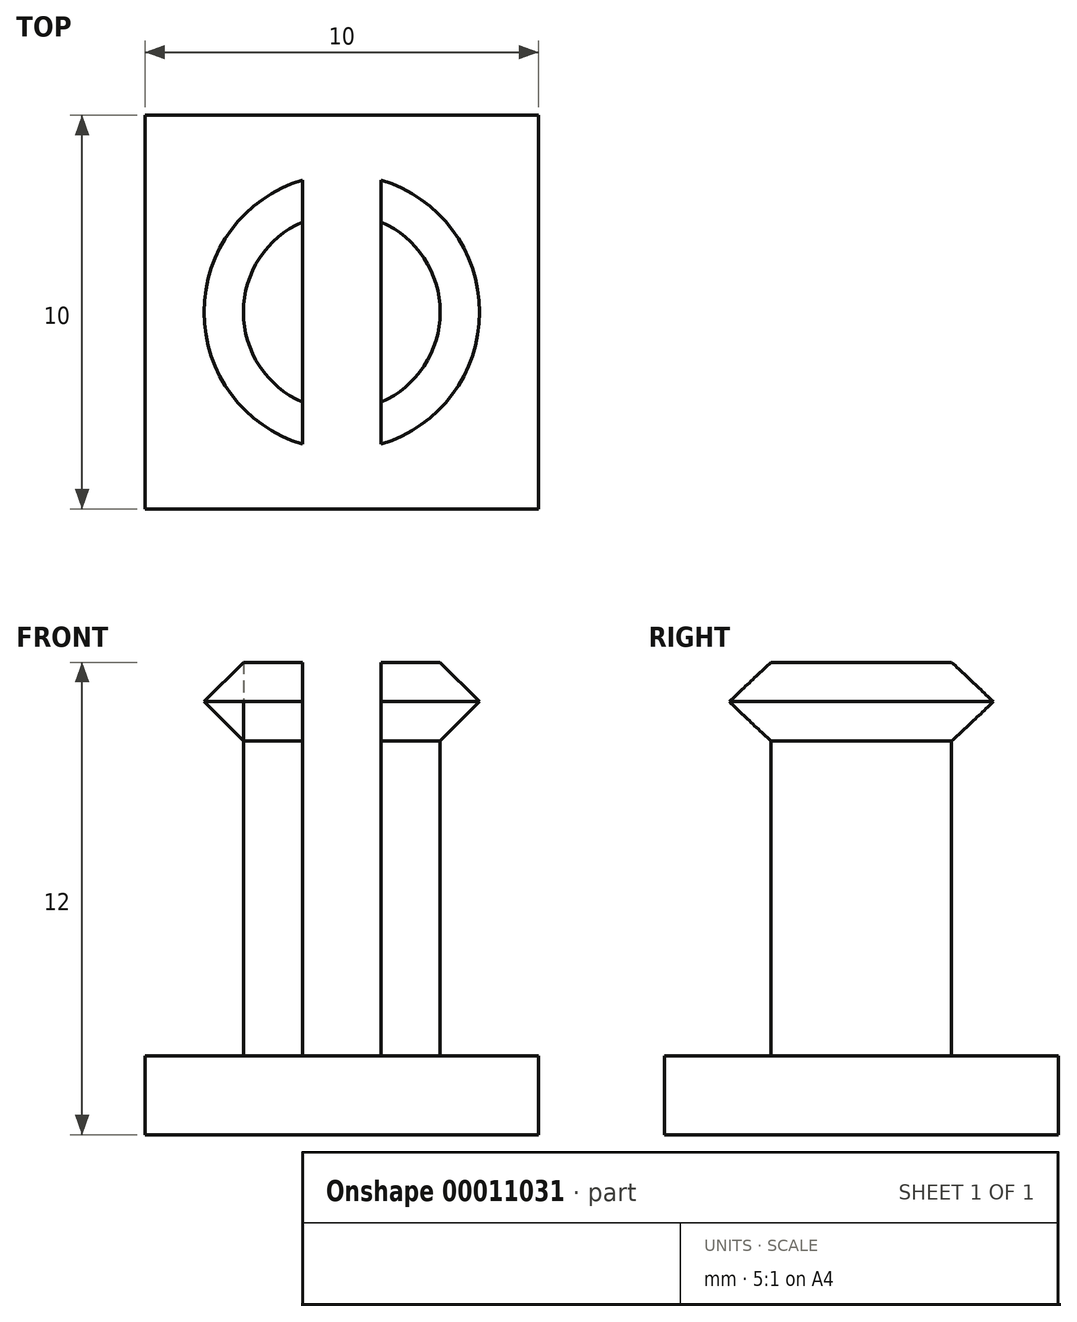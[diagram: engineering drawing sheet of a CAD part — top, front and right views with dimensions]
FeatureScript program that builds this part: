
annotation { "Feature Type Name" : "Feature", "Feature Type Description" : "" }
export const myFeature = defineFeature(function(context is Context, id is Id, definition is map)
    precondition{}
    {
        {
            var Q0;
            Q0=qCreatedBy(makeId("Top.planeOp"),FACE);
            var sketch = newSketch(context, id + "F0", { "sketchPlane" : qUnion([Q0])});
            skCircle(sketch, "E0", {"center": v(0, 0) * mm, "radius": 2.5 * mm});
            skLineSegment(sketch, "E1", {"start": v(0, 0) * mm, "end": v(-1, 0) * mm});
            skLineSegment(sketch, "E2", {"start": v(0, 0) * mm, "end": v(1, 0) * mm});
            skLineSegment(sketch, "E3", {"start": v(-1, 2.3) * mm, "end": v(-1, -2.3) * mm});
            skLineSegment(sketch, "E4", {"start": v(1, 2.3) * mm, "end": v(1, -2.3) * mm});
            skCircle(sketch, "E5.0", {"center": v(0, 0) * mm, "radius": 3.5 * mm});
            skLineSegment(sketch, "E6", {"start": v(-1, 2.3) * mm, "end": v(-1, 3.35) * mm});
            skLineSegment(sketch, "E7", {"start": v(1, 2.3) * mm, "end": v(1, 3.35) * mm});
            skLineSegment(sketch, "E8", {"start": v(1, -2.3) * mm, "end": v(1, -3.35) * mm});
            skLineSegment(sketch, "E9", {"start": v(-1, -2.3) * mm, "end": v(-1, -3.35) * mm});
            skLineSegment(sketch, "E10.bottom", {"start": v(-5, 5) * mm, "end": v(5, 5) * mm});
            skLineSegment(sketch, "E10.top", {"start": v(-5, -5) * mm, "end": v(5, -5) * mm});
            skLineSegment(sketch, "E10.left", {"start": v(-5, 5) * mm, "end": v(-5, -5) * mm});
            skLineSegment(sketch, "E10.right", {"start": v(5, 5) * mm, "end": v(5, -5) * mm});
            skSolve(sketch);
        }
        {
            var Q0;
            {var subQ0=sQuery(id+"F0.wireOp",EDGE,"E3");var subQ3=makeQuery(id+"F0.imprint","INTERSECT",VERTEX,{"derivedFrom":[sQuery(id+"F0.wireOp",EDGE,"E1"),subQ0]});Q0=makeQuery(id+"F0.imprint","IMPRINT",FACE,{"disambiguationData":[TD([[makeQuery(id+"F0.imprint","IMPRINT",EDGE,{"disambiguationData":[TD([[subQ3,1.0]])],"derivedFrom":subQ0}),-1.0]])]});}
            var Q1;
            {var subQ0=sQuery(id+"F0.wireOp",EDGE,"E4");var subQ3=makeQuery(id+"F0.imprint","INTERSECT",VERTEX,{"derivedFrom":[sQuery(id+"F0.wireOp",EDGE,"E2"),subQ0]});Q1=makeQuery(id+"F0.imprint","IMPRINT",FACE,{"disambiguationData":[TD([[makeQuery(id+"F0.imprint","IMPRINT",EDGE,{"disambiguationData":[TD([[subQ3,1.0]])],"derivedFrom":subQ0}),1.0]])]});}
            extrude(context, id + "F1", {"entities" : qUnion([Q0, Q1]), "depth" : 10 * mm});
        }
        {
            var Q0;
            {var subQ1=sQuery(id+"F0.wireOp",EDGE,"E6");Q0=makeQuery(id+"F0.imprint","IMPRINT",FACE,{"disambiguationData":[TD([[makeQuery(id+"F0.imprint","IMPRINT",EDGE,{"derivedFrom":subQ1}),1.0]])]});}
            var Q1;
            {var subQ1=sQuery(id+"F0.wireOp",EDGE,"E7");Q1=makeQuery(id+"F0.imprint","IMPRINT",FACE,{"disambiguationData":[TD([[makeQuery(id+"F0.imprint","IMPRINT",EDGE,{"derivedFrom":subQ1}),-1.0]])]});}
            extrude(context, id + "F2", {"entities" : qUnion([Q0, Q1]), "depth" : 10 * mm, "hasSecondDirection" : true, "secondDirectionOppositeDirection" : false, "secondDirectionDepth" : 8 * mm});
        }
        {
            var Q0;
            {var subQ0=sQuery(id+"F0.wireOp",EDGE,"E5.0");Q0=makeQuery(id+"F2.opExtrude","CAP_EDGE",EDGE,{"disambiguationData":[OSD([subQ0]),TDD([makeQuery(id+"F0.imprint","IMPRINT",EDGE,{"disambiguationData":[TD([[makeQuery(id+"F0.imprint","INTERSECT",VERTEX,{"derivedFrom":[subQ0,sQuery(id+"F0.wireOp",EDGE,"E6")]}),-1.0]])],"derivedFrom":subQ0})])],"isStart":false});}
            var Q1;
            {var subQ0=sQuery(id+"F0.wireOp",EDGE,"E5.0");Q1=makeQuery(id+"F2.opExtrude","CAP_EDGE",EDGE,{"disambiguationData":[OSD([subQ0]),TDD([makeQuery(id+"F0.imprint","IMPRINT",EDGE,{"disambiguationData":[TD([[makeQuery(id+"F0.imprint","INTERSECT",VERTEX,{"derivedFrom":[subQ0,sQuery(id+"F0.wireOp",EDGE,"E6")]}),-1.0]])],"derivedFrom":subQ0})])],"isStart":true});}
            var Q2;
            {var subQ0=sQuery(id+"F0.wireOp",EDGE,"E5.0");Q2=makeQuery(id+"F2.opExtrude","CAP_EDGE",EDGE,{"disambiguationData":[OSD([subQ0]),TDD([makeQuery(id+"F0.imprint","IMPRINT",EDGE,{"disambiguationData":[TD([[makeQuery(id+"F0.imprint","INTERSECT",VERTEX,{"derivedFrom":[subQ0,sQuery(id+"F0.wireOp",EDGE,"E7")]}),1.0]])],"derivedFrom":subQ0})])],"isStart":false});}
            var Q3;
            {var subQ0=sQuery(id+"F0.wireOp",EDGE,"E5.0");Q3=makeQuery(id+"F2.opExtrude","CAP_EDGE",EDGE,{"disambiguationData":[OSD([subQ0]),TDD([makeQuery(id+"F0.imprint","IMPRINT",EDGE,{"disambiguationData":[TD([[makeQuery(id+"F0.imprint","INTERSECT",VERTEX,{"derivedFrom":[subQ0,sQuery(id+"F0.wireOp",EDGE,"E7")]}),1.0]])],"derivedFrom":subQ0})])],"isStart":true});}
            chamfer(context, id + "F3", {"entities" : qUnion([Q0, Q1, Q2, Q3]), "width" : 1 * mm, "tangentPropagation" : true});
        }
        {
            var Q0;
            Q0=makeQuery(id+"F0.imprint","IMPRINT",FACE,{"disambiguationData":[TD([[makeQuery(id+"F0.imprint","IMPRINT",EDGE,{"derivedFrom":sQuery(id+"F0.wireOp",EDGE,"E10.bottom")}),-1.0]])]});
            var sketch = newSketch(context, id + "F4", { "sketchPlane" : qUnion([Q0])});
            skLineSegment(sketch, "E11.bottom", {"start": v(-5, -5) * mm, "end": v(5, -5) * mm});
            skLineSegment(sketch, "E11.top", {"start": v(-5, 5) * mm, "end": v(5, 5) * mm});
            skLineSegment(sketch, "E11.left", {"start": v(-5, -5) * mm, "end": v(-5, 5) * mm});
            skLineSegment(sketch, "E11.right", {"start": v(5, -5) * mm, "end": v(5, 5) * mm});
            skSolve(sketch);
        }
        {
            var Q0;
            Q0 = qSketchRegion(id + "F4", true);
            extrude(context, id + "F5", {"entities" : qUnion([Q0]), "oppositeDirection" : true, "depth" : 2 * mm});
        }
    });
